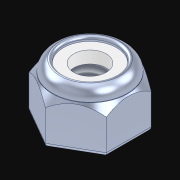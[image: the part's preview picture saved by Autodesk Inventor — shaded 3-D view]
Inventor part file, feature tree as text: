
AUTODESK INVENTOR PART (.ipt)
format: ipt  version: 2021.3 (Build 253353010, 353A)  size: 245,248 bytes
history: native  units: in
note: dims shown in document units (in); Inventor stores cm internally (conversion verified against a paired STEP export)
features: plane x2, other x1, imported_body x1, split x1, thread x1, extrude x1, fillet x1, sketch x1
ambient origin geometry x8: Origin, YZ Plane, XZ Plane, XY Plane, X Axis, Y Axis, Z Axis, Center Point
bodies: Body1 (feature_tree)
feature tree (9):
  parser-record x1  (decoder bookkeeping rows leaked as tree rows — omitted from the tree; the rows remain in map.json)
  imported_body  "Base1"
  plane  "Work Plane1"
  split  "Split1"
  thread  "Thread1"  [1 undecoded]
  plane  "Work Plane2"
  extrude  "Extrusion1"  Depth=0.015in TaperAngle=0.0deg
  fillet  "Fillet1"  Radius=0.015in
  sketch  "Sketch1"  dims[d2=-0.05in d4=0.053in d5=0.0in d6=0.015in]
note: 1 required parameter value undecoded (feature->parameter linkage not recoverable at this tier; creation-order binding heuristic only, values carry confidence <= 0.55)
